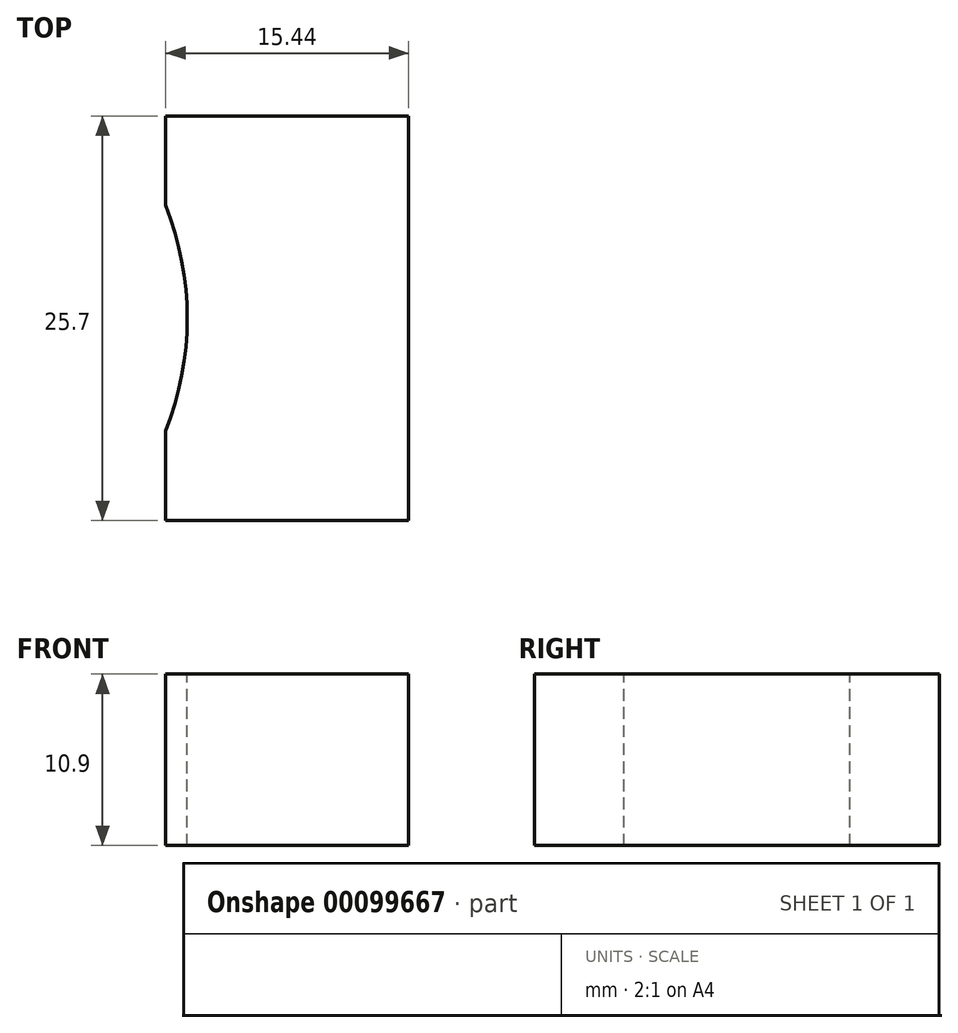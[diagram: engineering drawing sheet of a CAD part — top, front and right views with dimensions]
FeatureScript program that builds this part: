
annotation { "Feature Type Name" : "Feature", "Feature Type Description" : "" }
export const myFeature = defineFeature(function(context is Context, id is Id, definition is map)
    precondition{}
    {
        {
            var Q0;
            Q0=qCreatedBy(makeId("Front.planeOp"),FACE);
            var sketch = newSketch(context, id + "F0", { "sketchPlane" : qUnion([Q0])});
            skLineSegment(sketch, "E0.bottom", {"start": v(-15.44, 10.9) * mm, "end": v(0, 10.9) * mm});
            skLineSegment(sketch, "E0.top", {"start": v(-15.44, 0) * mm, "end": v(0, 0) * mm});
            skLineSegment(sketch, "E0.left", {"start": v(-15.44, 10.9) * mm, "end": v(-15.44, 0) * mm});
            skLineSegment(sketch, "E0.right", {"start": v(0, 10.9) * mm, "end": v(0, 0) * mm});
            skSolve(sketch);
        }
        {
            var Q0;
            Q0=makeQuery(id+"F0.imprint","IMPRINT",FACE,{"disambiguationData":[TD([[makeQuery(id+"F0.imprint","IMPRINT",EDGE,{"derivedFrom":sQuery(id+"F0.wireOp",EDGE,"E0.bottom")}),-1.0]])]});
            extrude(context, id + "F1", {"entities" : qUnion([Q0]), "depth" : 25.7 * mm});
        }
        {
            var Q0;
            Q0=makeQuery(id+"F1.opExtrude","SWEPT_FACE",FACE,{"disambiguationData":[OSD([sQuery(id+"F0.wireOp",EDGE,"E0.bottom")])]});
            var sketch = newSketch(context, id + "F2", { "sketchPlane" : qUnion([Q0])});
            skCircle(sketch, "E1", {"center": v(-33.57, -12.85) * mm, "radius": 19.5 * mm});
            skLineSegment(sketch, "E2", {"start": v(-7.72, 0) * mm, "end": v(-7.72, -25.7) * mm, "construction": true});
            skCircle(sketch, "E3.MirrorC", {"center": v(18.13, -12.85) * mm, "radius": 19.5 * mm});
            skSolve(sketch);
        }
        {
            var Q0;
            {var subQ0=sQuery(id+"F2.wireOp",EDGE,"E1");var subQ1=makeQuery(id+"F1.opExtrude","SWEPT_EDGE",EDGE,{"disambiguationData":[OSD([sQuery(id+"F0.wireOp",EDGE,"E0.bottom"),sQuery(id+"F0.wireOp",EDGE,"E0.left")])]});var subQ2=makeQuery(id+"F2.imprint","INTERSECT",VERTEX,{"disambiguationData":[OD(0.0)],"derivedFrom":[subQ1,subQ0]});Q0=makeQuery(id+"F2.imprint","IMPRINT",FACE,{"disambiguationData":[TD([[makeQuery(id+"F2.imprint","IMPRINT",EDGE,{"disambiguationData":[TD([[subQ2,1.0]])],"derivedFrom":subQ0}),1.0]])]});}
            var Q1;
            {var subQ0=sQuery(id+"F2.wireOp",EDGE,"E3.MirrorC");var subQ1=makeQuery(id+"F1.opExtrude","SWEPT_EDGE",EDGE,{"disambiguationData":[OSD([sQuery(id+"F0.wireOp",EDGE,"E0.bottom"),sQuery(id+"F0.wireOp",EDGE,"E0.right")])]});var subQ2=makeQuery(id+"F2.imprint","INTERSECT",VERTEX,{"disambiguationData":[OD(0.0)],"derivedFrom":[subQ1,subQ0]});Q1=makeQuery(id+"F2.imprint","IMPRINT",FACE,{"disambiguationData":[TD([[makeQuery(id+"F2.imprint","IMPRINT",EDGE,{"disambiguationData":[TD([[subQ2,1.0]])],"derivedFrom":subQ0}),-1.0]])]});}
            extrude(context, id + "F3", {"entities" : qUnion([Q0, Q1]), "operationType" : NewBodyOperationType.REMOVE, "endBound" : BoundingType.THROUGH_ALL, "oppositeDirection" : true, "depth" : 25 * mm});
        }
        {
            var Q0;
            Q0=qCreatedBy(makeId("Front.planeOp"),FACE);
            cPlane(context, id + "F4", {"entities" : qUnion([Q0]), "cplaneType" : CPlaneType.OFFSET, "offset" : 5 * mm, "width" : 150 * mm, "height" : 150 * mm});
        }
    });
